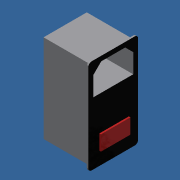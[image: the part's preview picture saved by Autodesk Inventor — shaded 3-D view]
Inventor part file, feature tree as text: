
AUTODESK INVENTOR PART (.ipt)
format: ipt  version: 2018 (Build 220112000, 112)  size: 134,656 bytes
history: native  units: mm
features: extrude x4, sketch x4, fillet x1
ambient origin geometry x8: Origin, YZ Plane, XZ Plane, XY Plane, X Axis, Y Axis, Z Axis, Center Point
bodies: Solid1 (feature_tree)
feature tree (9):
  extrude  "Extrusion1"  Depth=55.0mm
  extrude  "Extrusion2"  Depth=2.0mm
  fillet  "Fillet1"  Radius=2.0mm
  extrude  "Extrusion3"  Depth=2.0mm
  extrude  "Extrusion4"  Depth=2.0mm
  sketch  "Sketch1"  dims[d0=27.0mm d1=55.0mm]
  sketch  "Sketch2"  dims[d2=30.0mm d3=0.0mm d4=2.0mm d5=2.0mm]
  sketch  "Sketch3"  dims[d6=2.0mm d7=2.0mm]
  sketch  "Sketch4"  dims[d8=1.0mm d9=0.0mm d10=2.0mm d11=17.0mm d12=25.0mm d13=31.0mm d14=3.0mm d15=3.0mm d16=5.0mm d17=5.0mm d18=5.0mm d19=5.0mm d20=20.0mm d21=0.0mm d22=1.0mm d23=0.0mm]
